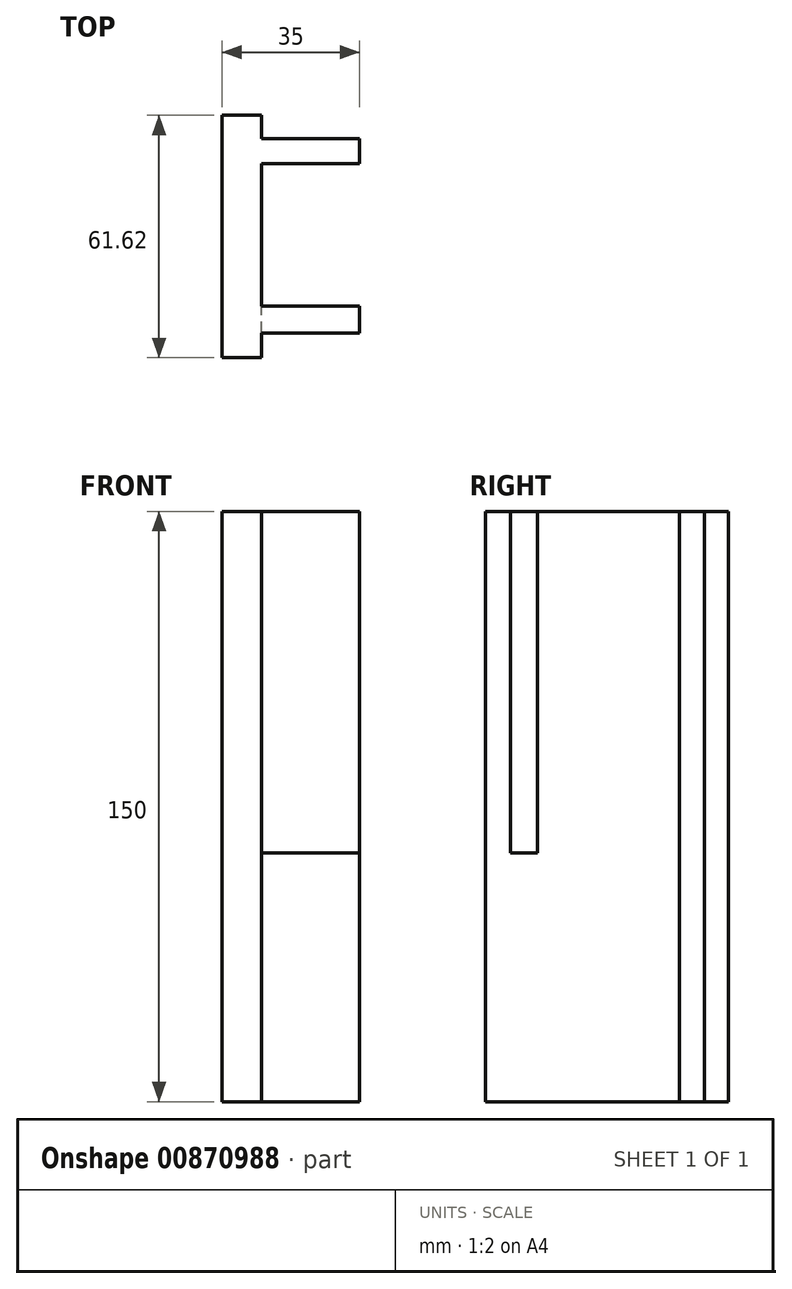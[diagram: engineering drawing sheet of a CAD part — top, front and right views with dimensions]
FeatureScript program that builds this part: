
annotation { "Feature Type Name" : "Feature", "Feature Type Description" : "" }
export const myFeature = defineFeature(function(context is Context, id is Id, definition is map)
    precondition{}
    {
        {
            var Q0;
            Q0=qCreatedBy(makeId("Top.planeOp"),FACE);
            var sketch = newSketch(context, id + "F0", { "sketchPlane" : qUnion([Q0])});
            skLineSegment(sketch, "E0.bottom", {"start": v(-19.8, -22.14) * mm, "end": v(-9.8, -22.14) * mm});
            skLineSegment(sketch, "E0.top", {"start": v(-19.8, -42.14) * mm, "end": v(-9.8, -42.14) * mm});
            skLineSegment(sketch, "E0.left", {"start": v(-19.8, -22.14) * mm, "end": v(-19.8, -42.14) * mm});
            skLineSegment(sketch, "E0.right", {"start": v(-9.8, -22.14) * mm, "end": v(-9.8, -42.14) * mm});
            skLineSegment(sketch, "E1.bottom", {"start": v(-9.8, -22.14) * mm, "end": v(-9.8, -22.14) * mm});
            skLineSegment(sketch, "E1.top", {"start": v(-9.8, 19.48) * mm, "end": v(-9.8, 19.48) * mm});
            skLineSegment(sketch, "E1.left", {"start": v(-9.8, -22.14) * mm, "end": v(-9.8, 19.48) * mm});
            skLineSegment(sketch, "E1.right", {"start": v(-9.8, -22.14) * mm, "end": v(-9.8, 19.48) * mm});
            skLineSegment(sketch, "E2.bottom", {"start": v(-19.8, -22.14) * mm, "end": v(-19.8, -22.14) * mm});
            skLineSegment(sketch, "E2.top", {"start": v(-19.8, 19.48) * mm, "end": v(-19.8, 19.48) * mm});
            skLineSegment(sketch, "E2.left", {"start": v(-19.8, -22.14) * mm, "end": v(-19.8, 19.48) * mm});
            skLineSegment(sketch, "E2.right", {"start": v(-19.8, -22.14) * mm, "end": v(-19.8, 19.48) * mm});
            skLineSegment(sketch, "E3.bottom", {"start": v(-9.8, 19.48) * mm, "end": v(-19.8, 19.48) * mm});
            skLineSegment(sketch, "E3.top", {"start": v(-9.8, 19.48) * mm, "end": v(-19.8, 19.48) * mm});
            skSolve(sketch);
        }
        {
            var Q0;
            Q0 = qSketchRegion(id + "F0", true);
            var Q1;
            Q1=makeQuery(id+"F0.imprint","IMPRINT",FACE,{"disambiguationData":[TD([[makeQuery(id+"F0.imprint","IMPRINT",EDGE,{"derivedFrom":sQuery(id+"F0.wireOp",EDGE,"E0.bottom")}),1.0]])]});
            extrude(context, id + "F1", {"entities" : qUnion([Q0, Q1]), "depth" : 150 * mm, "offsetDistance" : 25 * mm});
        }
        {
            var Q0;
            Q0=makeQuery(id+"F1.opExtrude","SWEPT_FACE",FACE,{"disambiguationData":[OSD([sQuery(id+"F0.wireOp",EDGE,"E0.right"),sQuery(id+"F0.wireOp",EDGE,"E1.right")])]});
            var sketch = newSketch(context, id + "F2", { "sketchPlane" : qUnion([Q0])});
            skLineSegment(sketch, "E4.bottom", {"start": v(-35.89, 63.15) * mm, "end": v(-29.04, 63.15) * mm});
            skLineSegment(sketch, "E4.top", {"start": v(-35.89, 150) * mm, "end": v(-29.04, 150) * mm});
            skLineSegment(sketch, "E4.left", {"start": v(-35.89, 63.15) * mm, "end": v(-35.89, 150) * mm});
            skLineSegment(sketch, "E4.right", {"start": v(-29.04, 63.15) * mm, "end": v(-29.04, 150) * mm});
            skLineSegment(sketch, "E5.bottom", {"start": v(7.13, 150) * mm, "end": v(13.48, 150) * mm});
            skLineSegment(sketch, "E5.top", {"start": v(7.13, 0) * mm, "end": v(13.48, 0) * mm});
            skLineSegment(sketch, "E5.left", {"start": v(7.13, 150) * mm, "end": v(7.13, 0) * mm});
            skLineSegment(sketch, "E5.right", {"start": v(13.48, 150) * mm, "end": v(13.48, 0) * mm});
            skSolve(sketch);
        }
        {
            var Q0;
            Q0=makeQuery(id+"F2.imprint","IMPRINT",FACE,{"disambiguationData":[TD([[makeQuery(id+"F2.imprint","IMPRINT",EDGE,{"derivedFrom":sQuery(id+"F2.wireOp",EDGE,"E5.bottom")}),1.0]])]});
            var Q1;
            Q1=makeQuery(id+"F2.imprint","IMPRINT",FACE,{"disambiguationData":[TD([[makeQuery(id+"F2.imprint","IMPRINT",EDGE,{"derivedFrom":sQuery(id+"F2.wireOp",EDGE,"E4.bottom")}),1.0]])]});
            extrude(context, id + "F3", {"entities" : qUnion([Q0, Q1]), "operationType" : NewBodyOperationType.ADD, "depth" : 25 * mm, "offsetDistance" : 25 * mm});
        }
    });
